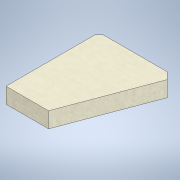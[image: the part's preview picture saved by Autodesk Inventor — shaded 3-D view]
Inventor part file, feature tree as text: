
AUTODESK INVENTOR PART (.ipt)
format: ipt  version: 2021 (Build 250183000, 183)  size: 108,544 bytes
history: native  units: mm
features: extrude x1, sketch x1
ambient origin geometry x8: Origin, YZ Plane, XZ Plane, XY Plane, X Axis, Y Axis, Z Axis, Center Point
bodies: Solid1 (feature_tree)
feature tree (2):
  extrude  "Extrusion1"  Depth=13.7mm
  sketch  "Sketch1"  dims[d0=3.5mm d1=3.5mm d2=81.4mm d3=37.2mm d4=65.5mm d5=59.65mm d6=13.7mm d7=0.0mm]
